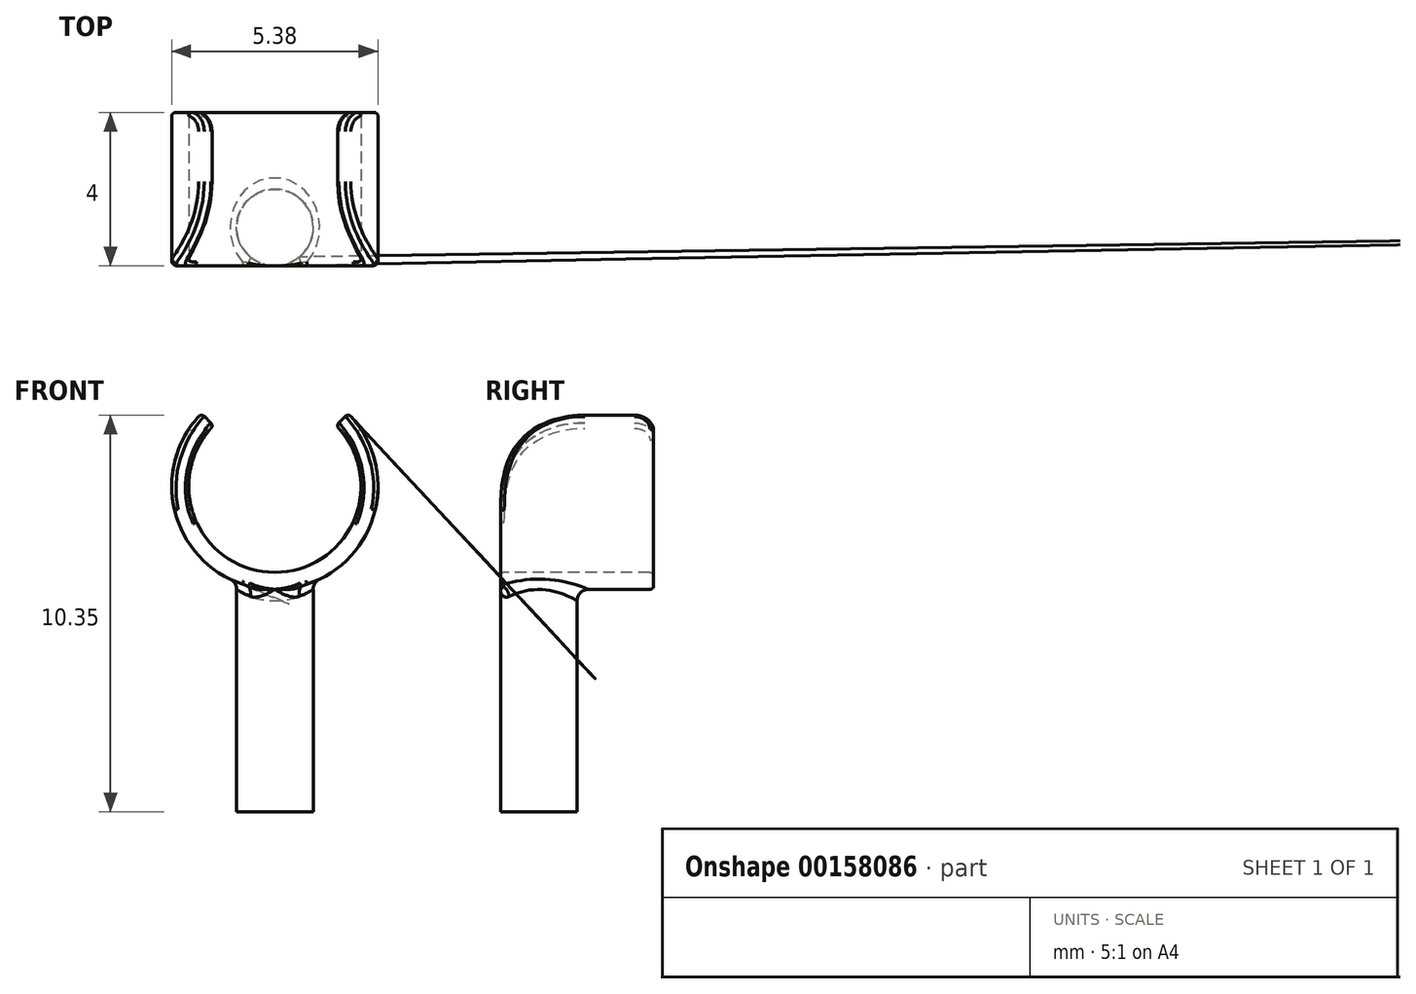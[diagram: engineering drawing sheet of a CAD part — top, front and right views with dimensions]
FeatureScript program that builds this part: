
annotation { "Feature Type Name" : "Feature", "Feature Type Description" : "" }
export const myFeature = defineFeature(function(context is Context, id is Id, definition is map)
    precondition{}
    {
        {
            var Q0;
            Q0=qCreatedBy(makeId("Top.planeOp"),FACE);
            var sketch = newSketch(context, id + "F0", { "sketchPlane" : qUnion([Q0])});
            skCircle(sketch, "E0", {"center": v(0, 0) * mm, "radius": 1 * mm});
            skSolve(sketch);
        }
        {
            var Q0;
            Q0=makeQuery(id+"F0.imprint","IMPRINT",FACE,{"disambiguationData":[TD([[makeQuery(id+"F0.imprint","IMPRINT",EDGE,{"derivedFrom":sQuery(id+"F0.wireOp",EDGE,"E0")}),1.0]])]});
            extrude(context, id + "F1", {"entities" : qUnion([Q0]), "depth" : 6 * mm});
        }
        {
            var Q0;
            Q0=qCreatedBy(makeId("Front.planeOp"),FACE);
            cPlane(context, id + "F2", {"entities" : qUnion([Q0]), "cplaneType" : CPlaneType.OFFSET, "offset" : 1 * mm, "width" : 150 * mm, "height" : 150 * mm});
        }
        {
            var Q0;
            Q0=qCreatedBy(id+"F2.planeOp",FACE);
            var sketch = newSketch(context, id + "F3", { "sketchPlane" : qUnion([Q0])});
            skArc(sketch, "E1", {"start": v(-1.6, 10.08) * mm, "mid": v(0, 6.25) * mm, "end": v(1.6, 10.08) * mm});
            skArc(sketch, "E2", {"start": v(-1.6, 10.67) * mm, "mid": v(0, 5.8) * mm, "end": v(1.6, 10.67) * mm});
            skLineSegment(sketch, "E3.0", {"start": v(-1, 6) * mm, "end": v(1, 6) * mm});
            skLineSegment(sketch, "E4", {"start": v(0, 8.5) * mm, "end": v(2.76, 11.23) * mm});
            skLineSegment(sketch, "E5", {"start": v(0, 8.5) * mm, "end": v(-2.69, 11.16) * mm});
            skLineSegment(sketch, "E6", {"start": v(-1.6, 10.08) * mm, "end": v(-1.6, 10.67) * mm});
            skLineSegment(sketch, "E7", {"start": v(1.6, 10.08) * mm, "end": v(1.6, 10.67) * mm});
            skSolve(sketch);
        }
        {
            var Q0;
            {var subQ2=sQuery(id+"F3.wireOp",EDGE,"E1");Q0=makeQuery(id+"F3.imprint","IMPRINT",FACE,{"disambiguationData":[TD([[makeQuery(id+"F3.imprint","IMPRINT",EDGE,{"derivedFrom":subQ2}),-1.0]])]});}
            var Q1;
            {var subQ0=sQuery(id+"F3.wireOp",EDGE,"E3.0");Q1=makeQuery(id+"F3.imprint","IMPRINT",FACE,{"disambiguationData":[TD([[makeQuery(id+"F3.imprint","IMPRINT",EDGE,{"derivedFrom":subQ0}),-1.0]])]});}
            extrude(context, id + "F4", {"entities" : qUnion([Q0, Q1]), "operationType" : NewBodyOperationType.ADD, "oppositeDirection" : true, "depth" : 4 * mm});
        }
        {
            var Q0;
            Q0=makeQuery(id+"F4.boolean.opBoolean","INTERSECT",EDGE,{"derivedFrom":[makeQuery(id+"F1.opExtrude","SWEPT_FACE",FACE,{"disambiguationData":[OSD([sQuery(id+"F0.wireOp",EDGE,"E0")])]}),makeQuery(id+"F4.opExtrude","SWEPT_FACE",FACE,{"disambiguationData":[OSD([sQuery(id+"F3.wireOp",EDGE,"E2")])]})]});
            fillet(context, id + "F5", {"entities" : qUnion([Q0]), "radius" : 0.3 * mm, "tangentPropagation" : true, "allowEdgeOverflow" : false});
        }
        {
            var Q0;
            Q0=makeQuery(id+"F4.opExtrude","CAP_EDGE",EDGE,{"disambiguationData":[OSD([sQuery(id+"F3.wireOp",EDGE,"E5")])],"isStart":true});
            var Q1;
            Q1=makeQuery(id+"F4.opExtrude","CAP_EDGE",EDGE,{"disambiguationData":[OSD([sQuery(id+"F3.wireOp",EDGE,"E4")])],"isStart":true});
            fillet(context, id + "F6", {"entities" : qUnion([Q0, Q1]), "radius" : 2.2 * mm, "tangentPropagation" : true, "allowEdgeOverflow" : false});
        }
        {
            var Q0;
            Q0=makeQuery(id+"F4.opExtrude","CAP_EDGE",EDGE,{"disambiguationData":[OSD([sQuery(id+"F3.wireOp",EDGE,"E4")])],"isStart":false});
            var Q1;
            Q1=makeQuery(id+"F4.opExtrude","CAP_EDGE",EDGE,{"disambiguationData":[OSD([sQuery(id+"F3.wireOp",EDGE,"E5")])],"isStart":false});
            fillet(context, id + "F7", {"entities" : qUnion([Q0, Q1]), "radius" : 0.5 * mm, "tangentPropagation" : true, "allowEdgeOverflow" : false});
        }
        {
            var Q0;
            Q0=makeQuery(id+"F4.opExtrude","CAP_EDGE",EDGE,{"disambiguationData":[OSD([sQuery(id+"F3.wireOp",EDGE,"E2")])],"isStart":false});
            var Q1;
            Q1=makeQuery(id+"F4.opExtrude","CAP_EDGE",EDGE,{"disambiguationData":[OSD([sQuery(id+"F3.wireOp",EDGE,"E1")])],"isStart":false});
            fillet(context, id + "F8", {"entities" : qUnion([Q0, Q1]), "radius" : 0.1 * mm, "tangentPropagation" : true, "allowEdgeOverflow" : false});
        }
    });
